# Revit family: 01-2553-11 JABONERA VIDRIO METALICA (EVO) PORTOBELLO
name_source: partatom
category: Plumbing Fixtures
revit_build: Autodesk Revit 2018 (Build: 20170223_1515(x64)
units: mm (PartAtom-declared; Revit-internal decimal feet)

## family parameters
Cut with Voids When Loaded = No
Host = Face
OmniClass Number = 23.31.11.00
Part Type = Normal
Room Calculation Point = No
Round Connector Dimension = Use Diameter
Shared = No

## types (1)
- 01-2553-11
    Alto Soporte = 48.5 mm  [stored 0.159121 ft]
    Alto brazo = 69 mm  [stored 0.226378 ft]
    Alto jabonera = 37 mm
    Ancho Soporte = 33 mm
    CW Connection = Yes
    Default Elevation = 0 mm  [stored 0 ft]
    Description = Jabonera
    Diametro = 109 mm  [stored 0.357612 ft]
    HW Connection = Yes
    Link Ficha Tecnica = http://infotecnica.gricol.com
    Manufacturer = Gricol
    Metal laton cromado = Metal Laton Cromado
    Model = 01-2553-11
    Product Name = JABONERA VIDRIO METALICA (EVO) PORTOBELLO
    Type Image = JABONERA VIDRIO METALICA PORTOBELLO.JPG
    URL = https://www.gricol.com
    Vent Connection = No
    Vidrio esmerilado = Vidrio Esmerilado
    Waste Connection = No

note: [stored X ft] marks values corroborated as IEEE doubles in the binary element streams (Revit-internal decimal feet)

## geometry (parser evidence)
native form markers: Blend x2, Sweep x2
no freeform markers — native parametric forms only
